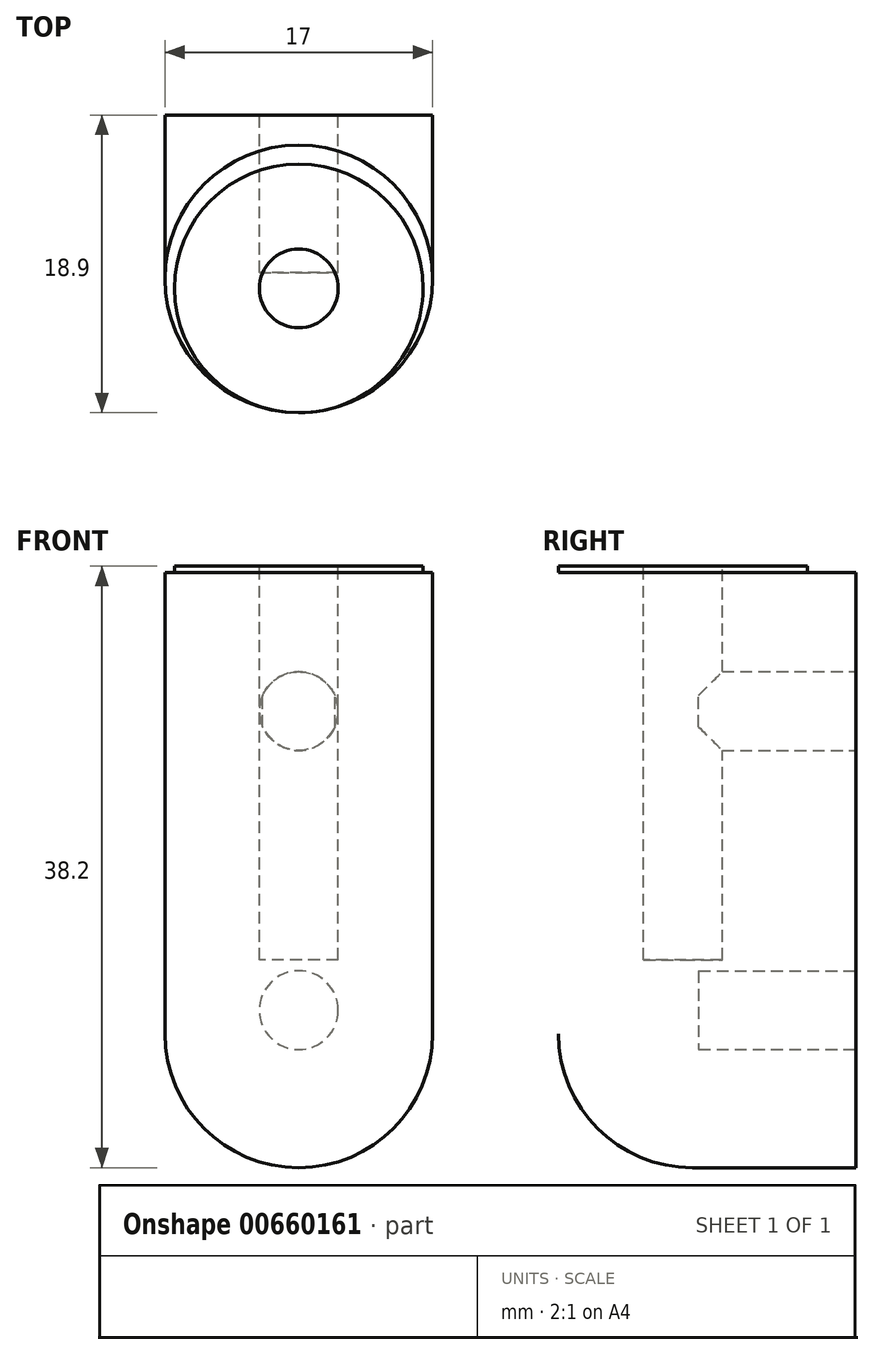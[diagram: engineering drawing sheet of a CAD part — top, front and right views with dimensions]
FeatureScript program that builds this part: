
annotation { "Feature Type Name" : "Feature", "Feature Type Description" : "" }
export const myFeature = defineFeature(function(context is Context, id is Id, definition is map)
    precondition{}
    {
        {
            var Q0;
            Q0=qCreatedBy(makeId("Front.planeOp"),FACE);
            var sketch = newSketch(context, id + "F0", { "sketchPlane" : qUnion([Q0])});
            skLineSegment(sketch, "E0.bottom", {"start": v(8.5, 0) * mm, "end": v(-8.5, 0) * mm});
            skLineSegment(sketch, "E0.top", {"start": v(8.5, 29.3) * mm, "end": v(-8.5, 29.3) * mm});
            skLineSegment(sketch, "E0.left", {"start": v(8.5, 0) * mm, "end": v(8.5, 29.3) * mm});
            skLineSegment(sketch, "E0.right", {"start": v(-8.5, 0) * mm, "end": v(-8.5, 29.3) * mm});
            skCircle(sketch, "E1", {"center": v(0, 0) * mm, "radius": 8.5 * mm});
            skSolve(sketch);
        }
        {
            var Q0;
            Q0=makeQuery(id+"F0.imprint","IMPRINT",FACE,{"disambiguationData":[TD([[makeQuery(id+"F0.imprint","IMPRINT",EDGE,{"derivedFrom":sQuery(id+"F0.wireOp",EDGE,"E0.top")}),1.0]])]});
            var Q1;
            {var subQ0=sQuery(id+"F0.wireOp",EDGE,"E0.bottom");Q1=makeQuery(id+"F0.imprint","IMPRINT",FACE,{"disambiguationData":[TD([[makeQuery(id+"F0.imprint","IMPRINT",EDGE,{"derivedFrom":subQ0}),-1.0]])]});}
            var Q2;
            {var subQ0=sQuery(id+"F0.wireOp",EDGE,"E0.bottom");Q2=makeQuery(id+"F0.imprint","IMPRINT",FACE,{"disambiguationData":[TD([[makeQuery(id+"F0.imprint","IMPRINT",EDGE,{"derivedFrom":subQ0}),1.0]])]});}
            extrude(context, id + "F1", {"entities" : qUnion([Q0, Q1, Q2]), "depth" : 18.9 * mm});
        }
        {
            var Q0;
            Q0=makeQuery(id+"F1.opExtrude","CAP_EDGE",EDGE,{"disambiguationData":[OSD([sQuery(id+"F0.wireOp",EDGE,"E0.left")])],"isStart":false});
            fillet(context, id + "F2", {"entities" : qUnion([Q0]), "radius" : 8.5 * mm, "tangentPropagation" : true, "allowEdgeOverflow" : false});
        }
        {
            var Q0;
            Q0=makeQuery(id+"F1.opExtrude","SWEPT_FACE",FACE,{"disambiguationData":[OSD([sQuery(id+"F0.wireOp",EDGE,"E0.top")])]});
            var sketch = newSketch(context, id + "F3", { "sketchPlane" : qUnion([Q0])});
            skCircle(sketch, "E2", {"center": v(0, -11) * mm, "radius": 7.9 * mm});
            skSolve(sketch);
        }
        {
            var Q0;
            Q0=makeQuery(id+"F3.imprint","IMPRINT",FACE,{"disambiguationData":[TD([[makeQuery(id+"F3.imprint","IMPRINT",EDGE,{"derivedFrom":sQuery(id+"F3.wireOp",EDGE,"E2")}),1.0]])]});
            extrude(context, id + "F4", {"entities" : qUnion([Q0]), "operationType" : NewBodyOperationType.ADD, "depth" : .4 * mm});
        }
        {
            var Q0;
            Q0=makeQuery(id+"F1.opExtrude","CAP_FACE",FACE,{"disambiguationData":[OSD([sQuery(id+"F0.wireOp",EDGE,"E0.top"),sQuery(id+"F0.wireOp",EDGE,"E0.left"),sQuery(id+"F0.wireOp",EDGE,"E0.right"),sQuery(id+"F0.wireOp",EDGE,"E1")])],"isStart":true});
            var sketch = newSketch(context, id + "F5", { "sketchPlane" : qUnion([Q0])});
            skCircle(sketch, "E3", {"center": v(0, 20.5) * mm, "radius": 2.5 * mm});
            skCircle(sketch, "E4", {"center": v(0, 1.5) * mm, "radius": 2.5 * mm});
            skSolve(sketch);
        }
        {
            var Q0;
            Q0=makeQuery(id+"F5.imprint","IMPRINT",FACE,{"disambiguationData":[TD([[makeQuery(id+"F5.imprint","IMPRINT",EDGE,{"derivedFrom":sQuery(id+"F5.wireOp",EDGE,"E3")}),1.0]])]});
            var Q1;
            Q1=makeQuery(id+"F5.imprint","IMPRINT",FACE,{"disambiguationData":[TD([[makeQuery(id+"F5.imprint","IMPRINT",EDGE,{"derivedFrom":sQuery(id+"F5.wireOp",EDGE,"E4")}),1.0]])]});
            extrude(context, id + "F6", {"entities" : qUnion([Q0, Q1]), "operationType" : NewBodyOperationType.REMOVE, "oppositeDirection" : true, "depth" : 10 * mm});
        }
        {
            var Q0;
            Q0=makeQuery(id+"F4.opExtrude","CAP_FACE",FACE,{"disambiguationData":[OSD([sQuery(id+"F3.wireOp",EDGE,"E2")])],"isStart":false});
            var sketch = newSketch(context, id + "F7", { "sketchPlane" : qUnion([Q0])});
            skCircle(sketch, "E5", {"center": v(0, -11) * mm, "radius": 2.5 * mm});
            skSolve(sketch);
        }
        {
            var Q0;
            Q0=makeQuery(id+"F7.imprint","IMPRINT",FACE,{"disambiguationData":[TD([[makeQuery(id+"F7.imprint","IMPRINT",EDGE,{"derivedFrom":sQuery(id+"F7.wireOp",EDGE,"E5")}),1.0]])]});
            extrude(context, id + "F8", {"entities" : qUnion([Q0]), "operationType" : NewBodyOperationType.REMOVE, "oppositeDirection" : true, "depth" : 25 * mm});
        }
    });
